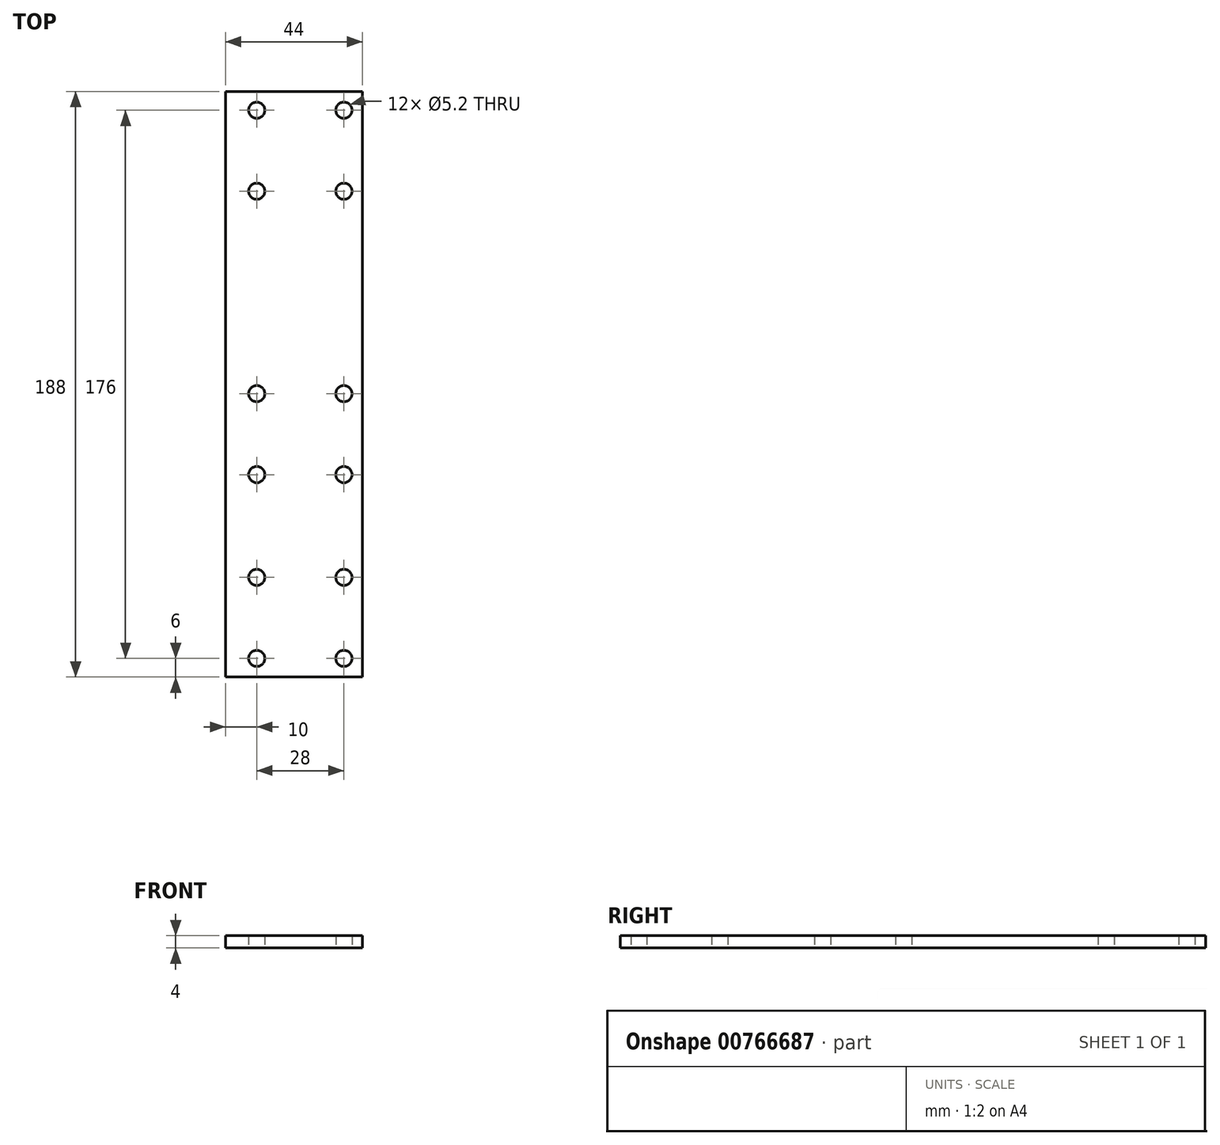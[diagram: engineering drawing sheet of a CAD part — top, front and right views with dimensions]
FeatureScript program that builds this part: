
annotation { "Feature Type Name" : "Feature", "Feature Type Description" : "" }
export const myFeature = defineFeature(function(context is Context, id is Id, definition is map)
    precondition{}
    {
        {
            var Q0;
            Q0=qCreatedBy(makeId("Top.planeOp"),FACE);
            var sketch = newSketch(context, id + "F0", { "sketchPlane" : qUnion([Q0])});
            skLineSegment(sketch, "E0.bottom", {"start": v(0, 0) * mm, "end": v(44, 0) * mm});
            skLineSegment(sketch, "E0.top", {"start": v(0, 188) * mm, "end": v(44, 188) * mm});
            skLineSegment(sketch, "E0.left", {"start": v(0, 0) * mm, "end": v(0, 188) * mm});
            skCircle(sketch, "E1", {"center": v(10, 182) * mm, "radius": 2.6 * mm});
            skCircle(sketch, "E2", {"center": v(38, 182) * mm, "radius": 2.6 * mm});
            skCircle(sketch, "E3", {"center": v(10, 156) * mm, "radius": 2.6 * mm});
            skCircle(sketch, "E4", {"center": v(38, 156) * mm, "radius": 2.6 * mm});
            skCircle(sketch, "E5", {"center": v(10, 91) * mm, "radius": 2.6 * mm});
            skCircle(sketch, "E6", {"center": v(38, 91) * mm, "radius": 2.6 * mm});
            skCircle(sketch, "E7", {"center": v(10, 65) * mm, "radius": 2.6 * mm});
            skCircle(sketch, "E8", {"center": v(38, 65) * mm, "radius": 2.6 * mm});
            skCircle(sketch, "E9", {"center": v(10, 32) * mm, "radius": 2.6 * mm});
            skCircle(sketch, "E10", {"center": v(38, 32) * mm, "radius": 2.6 * mm});
            skCircle(sketch, "E11", {"center": v(10, 6) * mm, "radius": 2.6 * mm});
            skCircle(sketch, "E12", {"center": v(38, 6) * mm, "radius": 2.6 * mm});
            skLineSegment(sketch, "E13", {"start": v(44, 188) * mm, "end": v(44, 0) * mm});
            skSolve(sketch);
        }
        {
            var Q0;
            Q0=makeQuery(id+"F0.imprint","IMPRINT",FACE,{"disambiguationData":[TD([[makeQuery(id+"F0.imprint","IMPRINT",EDGE,{"derivedFrom":sQuery(id+"F0.wireOp",EDGE,"E0.bottom")}),1.0]])]});
            extrude(context, id + "F1", {"entities" : qUnion([Q0]), "depth" : 4 * mm});
        }
    });
